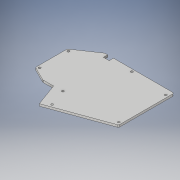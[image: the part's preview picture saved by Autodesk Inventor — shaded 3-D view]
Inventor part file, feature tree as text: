
AUTODESK INVENTOR PART (.ipt)
format: ipt  version: 2017 (Build 210142000, 142)  size: 183,808 bytes
history: native  units: in
note: dims shown in document units (in); Inventor stores cm internally (conversion verified against a paired STEP export)
features: fillet x6, extrude x3, sketch x3, projected_geometry x1
ambient origin geometry x8: Origin, YZ Plane, XZ Plane, XY Plane, X Axis, Y Axis, Z Axis, Center Point
bodies: Body1 (feature_tree)
feature tree (13):
  extrude  "Extrusion9"  Depth=1.2205in
  extrude  "Extrusion10"  Depth=0.1181in
  extrude  "Extrusion11"  Depth=0.1181in
  fillet  "Fillet1"  Radius=0.1181in
  fillet  "Fillet2"  Radius=0.3937in
  fillet  "Fillet3"  [1 undecoded]
  fillet  "Fillet4"  Radius=0.7874in
  fillet  "Fillet5"  Radius=0.5906in
  fillet  "Fillet6"  Radius=1.2992in
  sketch  "Sketch8"  dims[d73=0.1575in d129=1.2205in d131=0.8268in]
  sketch  "Sketch9"  dims[d132=0.1181in d133=0.0in d135=0.1181in]
  sketch  "Sketch10"  dims[d136=0.1181in d137=0.1181in d141=0.1181in d142=0.0in d147=0.3937in d151=0.0in d152=0.0in d154=0.7874in d155=0.5906in d162=1.2992in d163=0.7559in d164=3.7795in d165=0.1181in d166=0.1181in d169=0.1378in d179=0.1575in d180=0.2362in d181=0.315in d183=1.7323in d185=0.1181in d186=0.1378in d187=0.1378in d191=0.4724in d193=0.1575in d194=0.4724in d195=0.1575in d196=0.0787in d197=0.0787in d198=0.0787in d199=0.0787in d200=0.0787in d201=0.0787in d204=0.315in d205=0.1181in d206=2.1654in]
  projected_geometry  "Projected Loop2"
note: 1 required parameter value undecoded (feature->parameter linkage not recoverable at this tier; creation-order binding heuristic only, values carry confidence <= 0.55)
